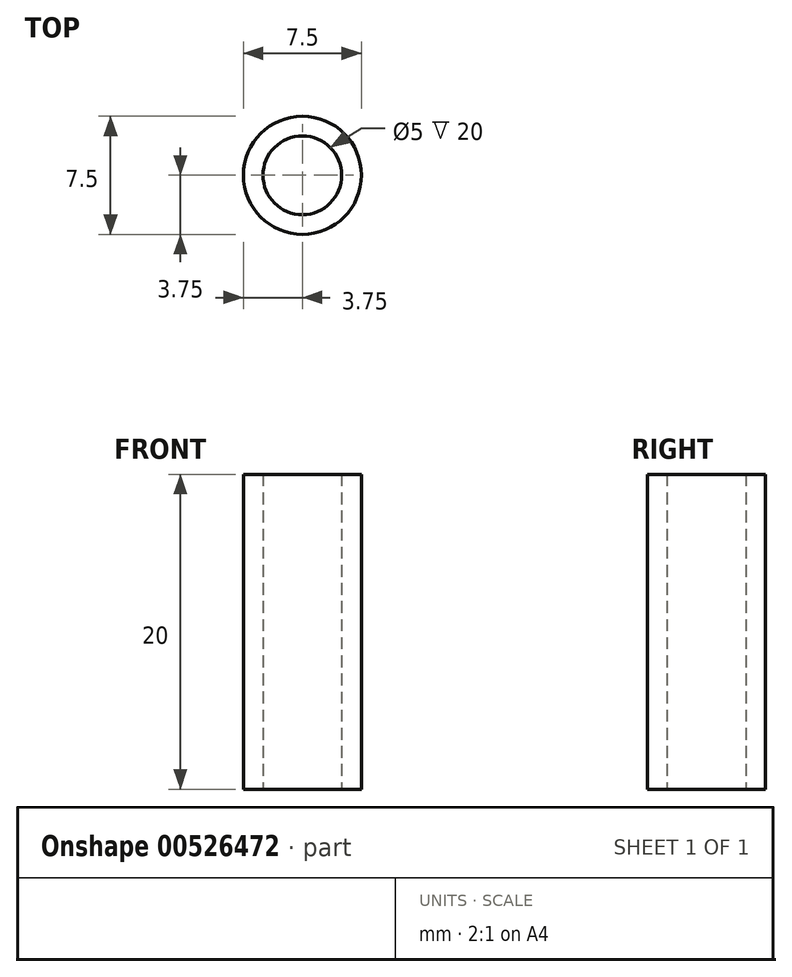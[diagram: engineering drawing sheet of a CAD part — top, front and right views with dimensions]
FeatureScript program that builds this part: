
annotation { "Feature Type Name" : "Feature", "Feature Type Description" : "" }
export const myFeature = defineFeature(function(context is Context, id is Id, definition is map)
    precondition{}
    {
        {
            var Q0;
            Q0=qCreatedBy(makeId("Top.planeOp"),FACE);
            var sketch = newSketch(context, id + "F0", { "sketchPlane" : qUnion([Q0])});
            skCircle(sketch, "E0", {"center": v(0, 0) * mm, "radius": 3.75 * mm});
            skCircle(sketch, "E1", {"center": v(0, 0) * mm, "radius": 2.5 * mm});
            skSolve(sketch);
        }
        {
            var Q0;
            Q0 = qSketchRegion(id + "F0", true);
            extrude(context, id + "F1", {"entities" : qUnion([Q0]), "depth" : 20 * mm, "offsetDistance" : 25 * mm});
        }
    });
